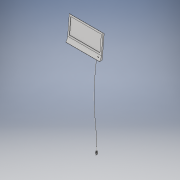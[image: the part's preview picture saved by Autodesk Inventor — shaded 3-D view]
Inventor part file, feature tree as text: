
AUTODESK INVENTOR PART (.ipt)
format: ipt  version: 2017 (Build 210142000, 142)  size: 560,640 bytes
history: native  units: in
note: dims shown in document units (in); Inventor stores cm internally (conversion verified against a paired STEP export)
features: sketch x14, extrude x12, other x8, plane x2, sweep x1, loft x1, mirror x1
ambient origin geometry x8: Origin, YZ Plane, XZ Plane, XY Plane, X Axis, Y Axis, Z Axis, Center Point
bodies: Solid1 (feature_tree), Solid2 (feature_tree), Solid3 (feature_tree)
feature tree (39):
  extrude  "block to cut from"  Depth=1.7188in
  extrude  "side view correct"  Depth=0.0104in
  extrude  "top view correct"  Depth=0.5841in
  plane  "Work Plane1"
  extrude  "slight top view correction"  Depth=0.0104in
  extrude  "screen"  TaperAngle=135.0deg  [1 undecoded]
  plane  "Work Plane2"
  extrude  "light cutout"  Depth=0.9583in
  sketch  "Sketch8"  dims[d17=0.0729in d19=0.1807in]
  extrude  "power indicator"  Depth=0.1807in
  extrude  "power button"  Depth=0.4271in TaperAngle=0.0deg
  extrude  "power symble"  Depth=0.3333in
  sweep  "wire"
  other  "plug bottom workplane"
  loft  "plug protection half"
  mirror  "plug protection other half"
  sketch  "Sketch17"  dims[d32=0.0781in d33=0.0833in]
  extrude  "hot wires"  Depth=0.0833in
  extrude  "ground wire"  Depth=0.0833in
  extrude  "addons for the hot wires"  Depth=0.3937in
  other  "ground pin round cut"
  other  "ground pin cut"
  other  "mate plane middle"
  other  "mate to back of stand"
  sketch  "Sketch1"  dims[d0=1.1771in d1=1.7188in]
  sketch  "Sketch2"  dims[d2=0.5527in d3=0.0in d4=0.0104in]
  sketch  "Sketch3"  dims[d6=0.3125in d7=0.5841in]
  sketch  "Sketch4"  dims[d8=0.6927in d12=0.0104in]
  sketch  "Sketch5"  dims[d13=0.0677in d14=135.0deg]
  sketch  "Sketch7"  dims[d15=0.1042in d16=0.9583in]
  sketch  "Sketch11"  dims[d20=5.6652in d21=0.4271in d22=0.0in]
  other  "cord line"
  sketch  "Sketch13"  dims[d23=0.3333in d24=0.3333in]
  other  "plug middle workplane"
  sketch  "Sketch15"  dims[d25=0.4271in d26=0.0in d27=90.0deg]
  sketch  "Sketch16"  dims[d28=0.0625in d29=1.4896in d30=0.0in]
  sketch  "Sketch18"  dims[d34=0.0781in d35=0.0833in]
  other  "Work Axis1"
  sketch  "Sketch19"  dims[d36=0.0208in d37=0.0in d38=0.0625in d40=45.0deg d49=0.0938in d50=0.0762in d51=0.021in d52=0.03in d53=0.0in d54=0.0749in d55=0.0013in d56=0.0185in d57=0.03in d58=0.0in d59=0.017in d60=0.0137in d61=0.0in d73=0.0019in d76=0.001in d77=0.001in d78=0.001in d79=0.0in d81=0.3827in d82=0.3937in d83=0.02in d84=0.3827in d85=0.0in d86=0.0in d87=0.0366in d88=0.0535in d89=0.0837in d92=0.0454in d93=0.0364in d97=0.0453in d111=0.3937in d130=0.0535in d131=0.0268in d132=0.0329in d133=0.0364in d134=0.0165in d135=0.0415in d136=0.0052in d137=0.0105in d139=0.0in d140=90.0deg d141=0.0in d142=90.0deg d143=0.0in d144=90.0deg d145=0.0045in d146=0.0189in d147=0.0189in d148=0.0208in d149=0.0125in d150=0.0157in d151=0.0115in d152=0.0558in d153=0.0in d154=0.0679in d155=0.0in d156=0.0064in d157=0.0047in d158=0.0098in d159=0.0141in d160=0.0679in d161=0.0in d162=90.0deg d164=0.0157in d165=90.0deg d166=0.02in]
note: 1 required parameter value undecoded (feature->parameter linkage not recoverable at this tier; creation-order binding heuristic only, values carry confidence <= 0.55)
